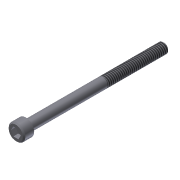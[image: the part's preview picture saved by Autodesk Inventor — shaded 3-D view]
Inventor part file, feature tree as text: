
AUTODESK INVENTOR PART (.ipt)
format: ipt  version: 2013 (Build 170138000, 138)  size: 95,744 bytes
history: native  units: in
note: dims shown in document units (in); Inventor stores cm internally (conversion verified against a paired STEP export)
features: extrude x3, sketch x3, chamfer x2, thread x1
ambient origin geometry x8: Origin, YZ Plane, XZ Plane, XY Plane, X Axis, Y Axis, Z Axis, Center Point
bodies: Solid1 (feature_tree)
feature tree (9):
  extrude  "Extrusion1"  Depth=0.164in TaperAngle=0.0deg
  extrude  "Extrusion2"  Depth=2.25in TaperAngle=0.0deg
  extrude  "Extrusion3"  Depth=0.08in TaperAngle=0.0deg
  thread  "Thread1"  [1 undecoded]
  chamfer  "Chamfer1"  Distance=0.02in Angle=45.0deg
  chamfer  "Chamfer2"  Distance=0.02in Angle=45.0deg
  sketch  "Sketch1"  dims[d0=0.27in d1=0.164in d2=0.0in]
  sketch  "Sketch2"  dims[d3=0.164in d4=2.25in d5=0.0in]
  sketch  "Sketch3"  dims[d6=0.1406in d7=0.08in d8=0.0in d9=1.0in d10=0.0in d11=0.02in d12=0.125in d13=45.0deg d14=0.02in d15=0.125in d16=45.0deg]
note: 1 required parameter value undecoded (feature->parameter linkage not recoverable at this tier; creation-order binding heuristic only, values carry confidence <= 0.55)
